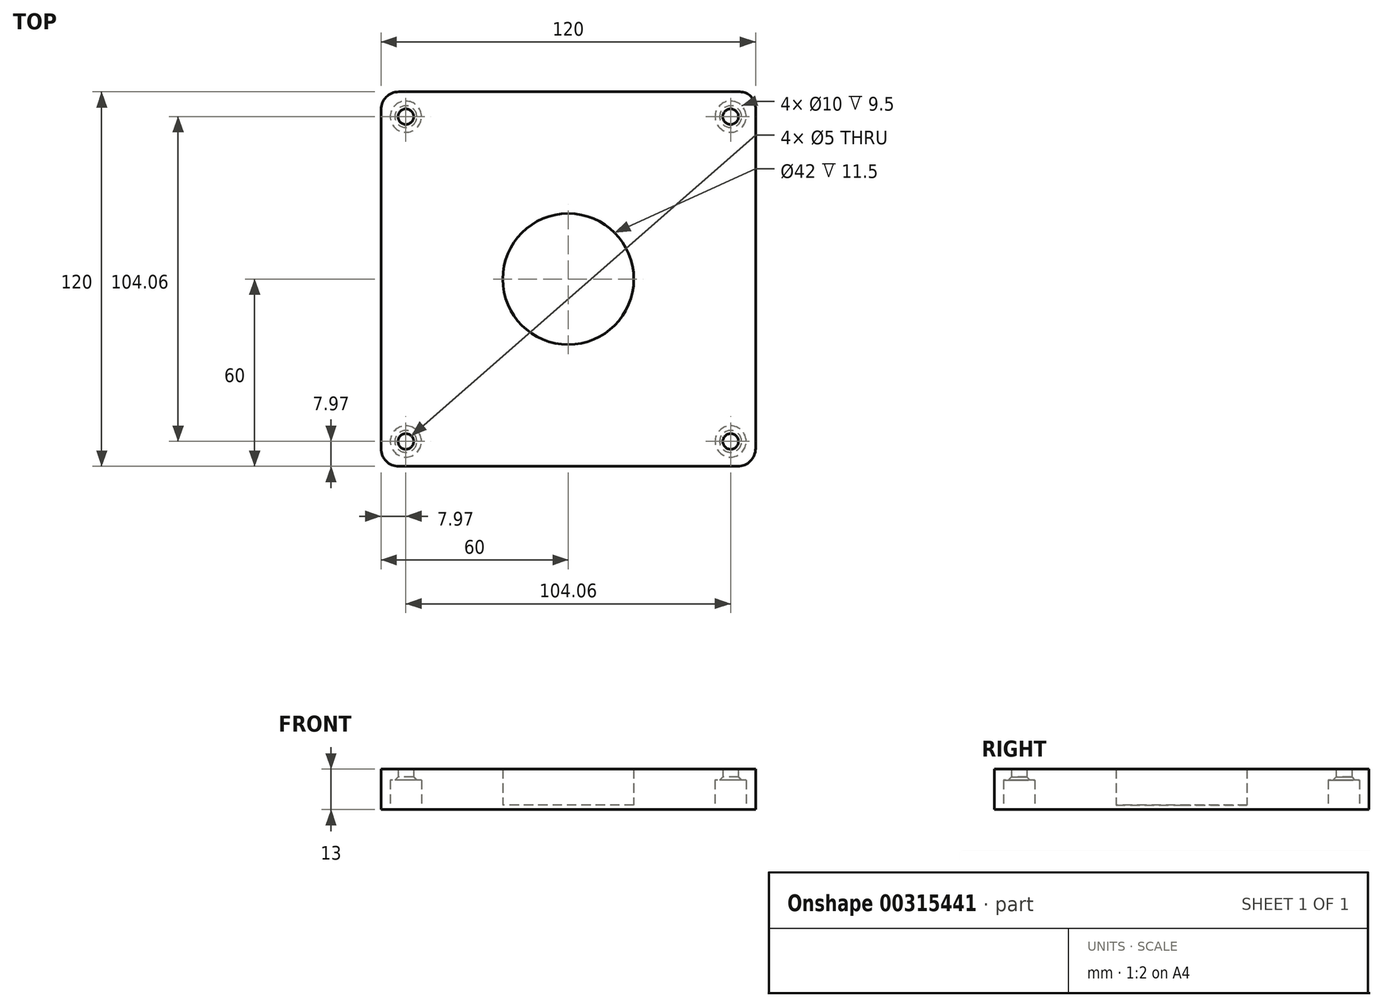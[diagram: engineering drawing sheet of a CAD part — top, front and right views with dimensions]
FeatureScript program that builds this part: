
annotation { "Feature Type Name" : "Feature", "Feature Type Description" : "" }
export const myFeature = defineFeature(function(context is Context, id is Id, definition is map)
    precondition{}
    {
        {
            var Q0;
            Q0=qCreatedBy(makeId("Top.planeOp"),FACE);
            var sketch = newSketch(context, id + "F0", { "sketchPlane" : qUnion([Q0])});
            skLineSegment(sketch, "E0.bottom", {"start": v(-54.3, 60) * mm, "end": v(55, 60) * mm});
            skLineSegment(sketch, "E0.top", {"start": v(-54.3, -60) * mm, "end": v(54.3, -60) * mm});
            skLineSegment(sketch, "E0.left", {"start": v(-60, 54.3) * mm, "end": v(-60, -54.3) * mm});
            skLineSegment(sketch, "E0.right", {"start": v(60, 55) * mm, "end": v(60, -54.3) * mm});
            skPoint(sketch, "E0.middle", {"position": v(0, 0) * mm});
            skPoint(sketch, "E1.visualSharp", {"position": v(-60, 60) * mm});
            skArc(sketch, "E1.filletArc", {"start": v(-54.3, 60) * mm, "mid": v(-58.33, 58.33) * mm, "end": v(-60, 54.3) * mm});
            skPoint(sketch, "E2.visualSharp", {"position": v(60, 60) * mm});
            skArc(sketch, "E2.filletArc", {"start": v(60, 55) * mm, "mid": v(58.54, 58.54) * mm, "end": v(55, 60) * mm});
            skPoint(sketch, "E3.visualSharp", {"position": v(60, -60) * mm});
            skArc(sketch, "E3.filletArc", {"start": v(54.3, -60) * mm, "mid": v(58.33, -58.33) * mm, "end": v(60, -54.3) * mm});
            skPoint(sketch, "E4.visualSharp", {"position": v(-60, -60) * mm});
            skArc(sketch, "E4.filletArc", {"start": v(-60, -54.3) * mm, "mid": v(-58.33, -58.33) * mm, "end": v(-54.3, -60) * mm});
            skCircle(sketch, "E5", {"center": v(0, 0) * mm, "radius": 21 * mm});
            skCircle(sketch, "E6", {"center": v(-52.03, 52.03) * mm, "radius": 2.5 * mm});
            skCircle(sketch, "E7", {"center": v(52.03, 52.03) * mm, "radius": 2.5 * mm});
            skCircle(sketch, "E8", {"center": v(52.03, -52.03) * mm, "radius": 2.5 * mm});
            skCircle(sketch, "E9", {"center": v(-52.03, -52.03) * mm, "radius": 2.5 * mm});
            skCircle(sketch, "E10.0", {"center": v(-52.03, -52.03) * mm, "radius": 5 * mm});
            skCircle(sketch, "E11.0", {"center": v(52.03, -52.03) * mm, "radius": 5 * mm});
            skCircle(sketch, "E12.0", {"center": v(52.03, 52.03) * mm, "radius": 5 * mm});
            skCircle(sketch, "E13.0", {"center": v(-52.03, 52.03) * mm, "radius": 5 * mm});
            skSolve(sketch);
        }
        {
            var Q0;
            Q0=makeQuery(id+"F0.imprint","IMPRINT",FACE,{"disambiguationData":[TD([[makeQuery(id+"F0.imprint","IMPRINT",EDGE,{"derivedFrom":sQuery(id+"F0.wireOp",EDGE,"E0.bottom")}),-1.0]])]});
            extrude(context, id + "F1", {"entities" : qUnion([Q0]), "depth" : 13 * mm});
        }
        {
            var Q0;
            Q0=makeQuery(id+"F0.imprint","IMPRINT",FACE,{"disambiguationData":[TD([[makeQuery(id+"F0.imprint","IMPRINT",EDGE,{"derivedFrom":sQuery(id+"F0.wireOp",EDGE,"E5")}),1.0]])]});
            extrude(context, id + "F2", {"entities" : qUnion([Q0]), "operationType" : NewBodyOperationType.ADD, "depth" : 1.5 * mm});
        }
        {
            var Q0;
            Q0=makeQuery(id+"F1.opExtrude","CAP_FACE",FACE,{"disambiguationData":[OSD([sQuery(id+"F0.wireOp",EDGE,"E0.bottom"),sQuery(id+"F0.wireOp",EDGE,"E0.top"),sQuery(id+"F0.wireOp",EDGE,"E0.left"),sQuery(id+"F0.wireOp",EDGE,"E0.right"),sQuery(id+"F0.wireOp",EDGE,"E1.filletArc"),sQuery(id+"F0.wireOp",EDGE,"E2.filletArc"),sQuery(id+"F0.wireOp",EDGE,"E3.filletArc"),sQuery(id+"F0.wireOp",EDGE,"E4.filletArc"),sQuery(id+"F0.wireOp",EDGE,"E5"),sQuery(id+"F0.wireOp",EDGE,"E10.0"),sQuery(id+"F0.wireOp",EDGE,"E11.0"),sQuery(id+"F0.wireOp",EDGE,"E12.0"),sQuery(id+"F0.wireOp",EDGE,"E13.0")])],"isStart":false});
            var sketch = newSketch(context, id + "F3", { "sketchPlane" : qUnion([Q0])});
            skSolve(sketch);
        }
        {
            var Q0;
            Q0=makeQuery(id+"F3.imprint","IMPRINT",FACE,{"disambiguationData":[TD([[makeQuery(id+"F3.imprint","IMPRINT",EDGE,{"derivedFrom":makeQuery(id+"F1.opExtrude","CAP_EDGE",EDGE,{"disambiguationData":[OSD([sQuery(id+"F0.wireOp",EDGE,"E11.0")])],"isStart":false})}),1.0]])]});
            var Q1;
            Q1=makeQuery(id+"F3.imprint","IMPRINT",FACE,{"disambiguationData":[TD([[makeQuery(id+"F3.imprint","IMPRINT",EDGE,{"derivedFrom":makeQuery(id+"F1.opExtrude","CAP_EDGE",EDGE,{"disambiguationData":[OSD([sQuery(id+"F0.wireOp",EDGE,"E10.0")])],"isStart":false})}),1.0]])]});
            var Q2;
            Q2=makeQuery(id+"F3.imprint","IMPRINT",FACE,{"disambiguationData":[TD([[makeQuery(id+"F3.imprint","IMPRINT",EDGE,{"derivedFrom":makeQuery(id+"F1.opExtrude","CAP_EDGE",EDGE,{"disambiguationData":[OSD([sQuery(id+"F0.wireOp",EDGE,"E13.0")])],"isStart":false})}),1.0]])]});
            var Q3;
            Q3=makeQuery(id+"F3.imprint","IMPRINT",FACE,{"disambiguationData":[TD([[makeQuery(id+"F3.imprint","IMPRINT",EDGE,{"derivedFrom":makeQuery(id+"F1.opExtrude","CAP_EDGE",EDGE,{"disambiguationData":[OSD([sQuery(id+"F0.wireOp",EDGE,"E12.0")])],"isStart":false})}),1.0]])]});
            extrude(context, id + "F4", {"entities" : qUnion([Q0, Q1, Q2, Q3]), "operationType" : NewBodyOperationType.ADD, "oppositeDirection" : true, "depth" : 3.5 * mm});
        }
        {
            var Q0;
            Q0=makeQuery(id+"F0.imprint","IMPRINT",FACE,{"disambiguationData":[TD([[makeQuery(id+"F0.imprint","IMPRINT",EDGE,{"derivedFrom":sQuery(id+"F0.wireOp",EDGE,"E9")}),1.0]])]});
            var Q1;
            Q1=makeQuery(id+"F0.imprint","IMPRINT",FACE,{"disambiguationData":[TD([[makeQuery(id+"F0.imprint","IMPRINT",EDGE,{"derivedFrom":sQuery(id+"F0.wireOp",EDGE,"E8")}),1.0]])]});
            var Q2;
            Q2=makeQuery(id+"F0.imprint","IMPRINT",FACE,{"disambiguationData":[TD([[makeQuery(id+"F0.imprint","IMPRINT",EDGE,{"derivedFrom":sQuery(id+"F0.wireOp",EDGE,"E7")}),1.0]])]});
            var Q3;
            Q3=makeQuery(id+"F0.imprint","IMPRINT",FACE,{"disambiguationData":[TD([[makeQuery(id+"F0.imprint","IMPRINT",EDGE,{"derivedFrom":sQuery(id+"F0.wireOp",EDGE,"E6")}),1.0]])]});
            extrude(context, id + "F5", {"entities" : qUnion([Q0, Q1, Q2, Q3]), "operationType" : NewBodyOperationType.REMOVE, "depth" : 27.6 * mm});
        }
        {
            var Q0;
            Q0=makeQuery(id+"F5.boolean.opBoolean","INTERSECT",EDGE,{"derivedFrom":[makeQuery(id+"F4.opExtrude","CAP_FACE",FACE,{"disambiguationData":[OSD([sQuery(id+"F0.wireOp",EDGE,"E12.0")])],"isStart":false}),makeQuery(id+"F5.opExtrude","SWEPT_FACE",FACE,{"disambiguationData":[OSD([sQuery(id+"F0.wireOp",EDGE,"E7")])]})]});
            var Q1;
            Q1=makeQuery(id+"F5.boolean.opBoolean","INTERSECT",EDGE,{"derivedFrom":[makeQuery(id+"F4.opExtrude","CAP_FACE",FACE,{"disambiguationData":[OSD([sQuery(id+"F0.wireOp",EDGE,"E13.0")])],"isStart":false}),makeQuery(id+"F5.opExtrude","SWEPT_FACE",FACE,{"disambiguationData":[OSD([sQuery(id+"F0.wireOp",EDGE,"E6")])]})]});
            var Q2;
            Q2=makeQuery(id+"F5.boolean.opBoolean","INTERSECT",EDGE,{"derivedFrom":[makeQuery(id+"F4.opExtrude","CAP_FACE",FACE,{"disambiguationData":[OSD([sQuery(id+"F0.wireOp",EDGE,"E11.0")])],"isStart":false}),makeQuery(id+"F5.opExtrude","SWEPT_FACE",FACE,{"disambiguationData":[OSD([sQuery(id+"F0.wireOp",EDGE,"E8")])]})]});
            var Q3;
            Q3=makeQuery(id+"F5.boolean.opBoolean","INTERSECT",EDGE,{"derivedFrom":[makeQuery(id+"F4.opExtrude","CAP_FACE",FACE,{"disambiguationData":[OSD([sQuery(id+"F0.wireOp",EDGE,"E10.0")])],"isStart":false}),makeQuery(id+"F5.opExtrude","SWEPT_FACE",FACE,{"disambiguationData":[OSD([sQuery(id+"F0.wireOp",EDGE,"E9")])]})]});
            chamfer(context, id + "F6", {"entities" : qUnion([Q0, Q1, Q2, Q3]), "width" : 1 * mm, "tangentPropagation" : true});
        }
    });
